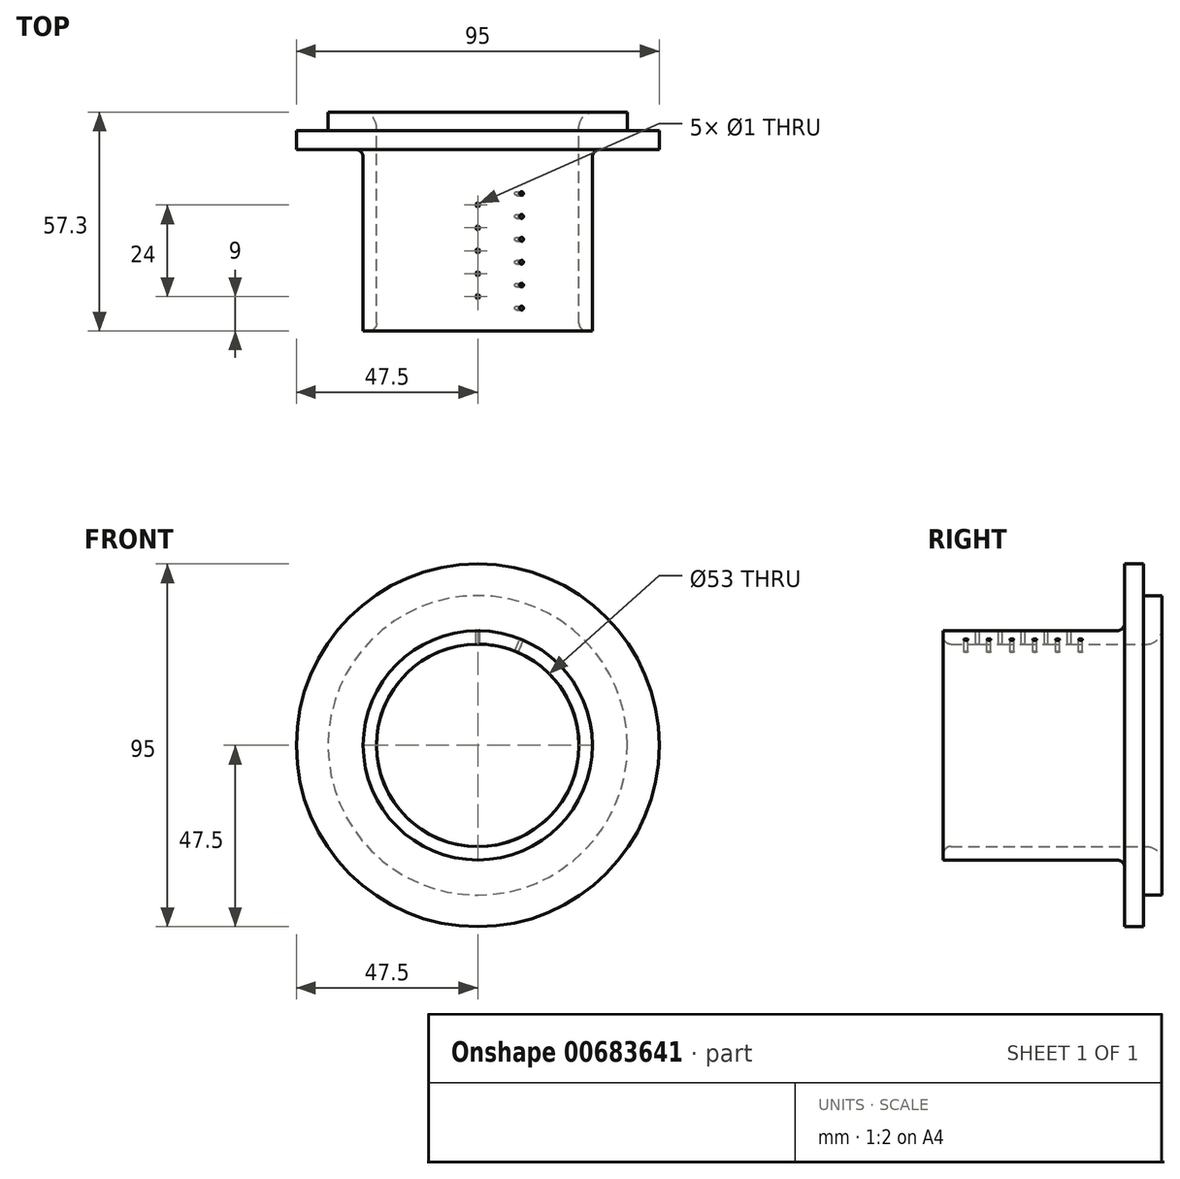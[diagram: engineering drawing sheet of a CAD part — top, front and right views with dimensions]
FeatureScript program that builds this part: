
annotation { "Feature Type Name" : "Feature", "Feature Type Description" : "" }
export const myFeature = defineFeature(function(context is Context, id is Id, definition is map)
    precondition{}
    {
        {
            var Q0;
            Q0=qCreatedBy(makeId("Right.planeOp"),FACE);
            var sketch = newSketch(context, id + "F0", { "sketchPlane" : qUnion([Q0])});
            skLineSegment(sketch, "E0", {"start": v(0, 39.2) * mm, "end": v(0, 47.5) * mm});
            skLineSegment(sketch, "E1", {"start": v(0, 47.5) * mm, "end": v(-5, 47.5) * mm});
            skLineSegment(sketch, "E2", {"start": v(-5, 47.5) * mm, "end": v(-5, 32) * mm});
            skLineSegment(sketch, "E3", {"start": v(-7, 30) * mm, "end": v(-52.5, 30) * mm});
            skLineSegment(sketch, "E4", {"start": v(0, 0) * mm, "end": v(-70.46, 0) * mm, "construction": true});
            skPoint(sketch, "E5.visualSharp", {"position": v(-5, 30) * mm});
            skArc(sketch, "E5.filletArc", {"start": v(-7, 30) * mm, "mid": v(-5.59, 30.59) * mm, "end": v(-5, 32) * mm});
            skLineSegment(sketch, "E6", {"start": v(0, 39.2) * mm, "end": v(4.8, 39.2) * mm});
            skLineSegment(sketch, "E7", {"start": v(4.8, 30.5) * mm, "end": v(4.8, 39.2) * mm});
            skLineSegment(sketch, "E8", {"start": v(0.8, 26.5) * mm, "end": v(-50.5, 26.5) * mm});
            skPoint(sketch, "E9.visualSharp", {"position": v(4.8, 26.5) * mm});
            skArc(sketch, "E9.filletArc", {"start": v(0.8, 26.5) * mm, "mid": v(3.63, 27.67) * mm, "end": v(4.8, 30.5) * mm});
            skLineSegment(sketch, "E10", {"start": v(-52.5, 30) * mm, "end": v(-52.5, 28.5) * mm});
            skPoint(sketch, "E11.visualSharp", {"position": v(-52.5, 26.5) * mm});
            skArc(sketch, "E11.filletArc", {"start": v(-52.5, 28.5) * mm, "mid": v(-51.91, 27.09) * mm, "end": v(-50.5, 26.5) * mm});
            skSolve(sketch);
        }
        {
            var Q0;
            Q0=makeQuery(id+"F0.imprint","IMPRINT",FACE,{"disambiguationData":[TD([[makeQuery(id+"F0.imprint","IMPRINT",EDGE,{"derivedFrom":sQuery(id+"F0.wireOp",EDGE,"E0")}),1.0]])]});
            var Q1;
            Q1=sQuery(id+"F0.wireOp",EDGE,"E4");
            revolve(context, id + "F1", {"entities" : qUnion([Q0]), "axis" : qUnion([Q1]), "revolveType" : RevolveType.FULL});
        }
        {
            var Q0;
            Q0=qCreatedBy(makeId("Top.planeOp"),FACE);
            cPlane(context, id + "F2", {"entities" : qUnion([Q0]), "cplaneType" : CPlaneType.OFFSET, "offset" : 30 * mm, "width" : 150 * mm, "height" : 150 * mm});
        }
        {
            var Q0;
            Q0=qCreatedBy(id+"F2.planeOp",FACE);
            var sketch = newSketch(context, id + "F3", { "sketchPlane" : qUnion([Q0])});
            skLineSegment(sketch, "E12", {"start": v(0, 15.34) * mm, "end": v(0, -7) * mm, "construction": true});
            skPoint(sketch, "E13", {"position": v(0, -16.5) * mm});
            skPoint(sketch, "E14", {"position": v(0, -19.5) * mm});
            skPoint(sketch, "E15", {"position": v(0, -22.5) * mm});
            skPoint(sketch, "E16", {"position": v(0, -25.5) * mm});
            skPoint(sketch, "E17", {"position": v(0, -28.5) * mm});
            skPoint(sketch, "E18", {"position": v(0, -31.5) * mm});
            skPoint(sketch, "E19", {"position": v(0, -34.5) * mm});
            skPoint(sketch, "E20", {"position": v(0, -37.5) * mm});
            skPoint(sketch, "E21", {"position": v(0, -40.5) * mm});
            skPoint(sketch, "E22", {"position": v(0, -43.5) * mm});
            skPoint(sketch, "E23", {"position": v(0, -46.5) * mm});
            skSolve(sketch);
        }
        {
            var Q0;
            Q0=sQuery(id+"F3.wireOp",VERTEX,"3c57dba0-33b4-4bc7-9758-ce83d420cd37");
            var Q1;
            Q1=sQuery(id+"F3.wireOp",VERTEX,"129ee109-2fb9-47cf-9f09-9b5d60d57f23");
            var Q2;
            Q2=sQuery(id+"F3.wireOp",VERTEX,"E13");
            var Q3;
            Q3=sQuery(id+"F3.wireOp",VERTEX,"E15");
            var Q4;
            Q4=sQuery(id+"F3.wireOp",VERTEX,"E17");
            var Q5;
            Q5=sQuery(id+"F3.wireOp",VERTEX,"E19");
            var Q6;
            Q6=sQuery(id+"F3.wireOp",VERTEX,"E21");
            var Q7;
            Q7=sQuery(id+"F3.wireOp",VERTEX,"E23");
            var Q8;
            Q8=makeQuery(id+"F1.opRevolve","SWEPT_BODY",BODY,{"disambiguationData":[OSD([sQuery(id+"F0.wireOp",EDGE,"E0"),sQuery(id+"F0.wireOp",EDGE,"E1"),sQuery(id+"F0.wireOp",EDGE,"E2"),sQuery(id+"F0.wireOp",EDGE,"E3"),sQuery(id+"F0.wireOp",EDGE,"cO9Nc2A4-NVQm-xS0q-1Dsc-YeXu757I9n1a"),sQuery(id+"F0.wireOp",EDGE,"AHbMODby-IzKW-ggdr-t5a6-sW0KFh31dXH3"),sQuery(id+"F0.wireOp",EDGE,"3d177a93-f1fe-4711-a7cb-48db8fccbb41.filletArc"),sQuery(id+"F0.wireOp",EDGE,"1b0b4968-23c5-4b4f-a7c4-7fd432a90d28.filletArc"),sQuery(id+"F0.wireOp",EDGE,"E5.filletArc")])]});
            hole(context, id + "F4", {"style" : HoleStyle.SIMPLE, "endStyle" : HoleEndStyle.BLIND, "holeDiameter" : 1 * mm, "majorDiameter" : 5 * mm, "holeDepth" : 5 * mm, "tappedDepth" : 12 * mm, "tapClearance" : 3, "startFromSketch" : true, "locations" : qUnion([Q0, Q1, Q2, Q3, Q4, Q5, Q6, Q7]), "scope" : qUnion([Q8])});
        }
        {
            var Q0;
            Q0=makeQuery(id+"F1.opRevolve","SWEPT_BODY",BODY,{"disambiguationData":[OSD([sQuery(id+"F0.wireOp",EDGE,"E0"),sQuery(id+"F0.wireOp",EDGE,"E1"),sQuery(id+"F0.wireOp",EDGE,"E2"),sQuery(id+"F0.wireOp",EDGE,"E3"),sQuery(id+"F0.wireOp",EDGE,"cO9Nc2A4-NVQm-xS0q-1Dsc-YeXu757I9n1a"),sQuery(id+"F0.wireOp",EDGE,"AHbMODby-IzKW-ggdr-t5a6-sW0KFh31dXH3"),sQuery(id+"F0.wireOp",EDGE,"3d177a93-f1fe-4711-a7cb-48db8fccbb41.filletArc"),sQuery(id+"F0.wireOp",EDGE,"1b0b4968-23c5-4b4f-a7c4-7fd432a90d28.filletArc"),sQuery(id+"F0.wireOp",EDGE,"E5.filletArc")])]});
            var Q1;
            Q1=makeQuery(id+"F1.opRevolve","SWEPT_EDGE",EDGE,{"disambiguationData":[OSD([sQuery(id+"F0.wireOp",EDGE,"E1"),sQuery(id+"F0.wireOp",EDGE,"E2")])]});
            transform(context, id + "F5", {"entities" : qUnion([Q0]), "transformType" : TransformType.ROTATION, "transformAxis" : qUnion([Q1]), "angle" : 22.5 * degree, "makeCopy" : false});
        }
        {
            var Q0;
            Q0=sQuery(id+"F3.wireOp",VERTEX,"524c31e7-7040-4c50-a11b-71827ce9c6f2");
            var Q1;
            Q1=sQuery(id+"F3.wireOp",VERTEX,"86c4b006-8a74-4096-b4f1-74f78bb031bc");
            var Q2;
            Q2=sQuery(id+"F3.wireOp",VERTEX,"E14");
            var Q3;
            Q3=sQuery(id+"F3.wireOp",VERTEX,"E16");
            var Q4;
            Q4=sQuery(id+"F3.wireOp",VERTEX,"E18");
            var Q5;
            Q5=sQuery(id+"F3.wireOp",VERTEX,"E20");
            var Q6;
            Q6=sQuery(id+"F3.wireOp",VERTEX,"E22");
            var Q7;
            Q7=makeQuery(id+"F1.opRevolve","SWEPT_BODY",BODY,{"disambiguationData":[OSD([sQuery(id+"F0.wireOp",EDGE,"E0"),sQuery(id+"F0.wireOp",EDGE,"E1"),sQuery(id+"F0.wireOp",EDGE,"E2"),sQuery(id+"F0.wireOp",EDGE,"E3"),sQuery(id+"F0.wireOp",EDGE,"cO9Nc2A4-NVQm-xS0q-1Dsc-YeXu757I9n1a"),sQuery(id+"F0.wireOp",EDGE,"AHbMODby-IzKW-ggdr-t5a6-sW0KFh31dXH3"),sQuery(id+"F0.wireOp",EDGE,"3d177a93-f1fe-4711-a7cb-48db8fccbb41.filletArc"),sQuery(id+"F0.wireOp",EDGE,"1b0b4968-23c5-4b4f-a7c4-7fd432a90d28.filletArc"),sQuery(id+"F0.wireOp",EDGE,"E5.filletArc")])]});
            hole(context, id + "F6", {"style" : HoleStyle.SIMPLE, "endStyle" : HoleEndStyle.BLIND, "holeDiameter" : 1 * mm, "majorDiameter" : 5 * mm, "holeDepth" : 5 * mm, "tappedDepth" : 12 * mm, "tapClearance" : 3, "startFromSketch" : true, "locations" : qUnion([Q0, Q1, Q2, Q3, Q4, Q5, Q6]), "scope" : qUnion([Q7])});
        }
    });
